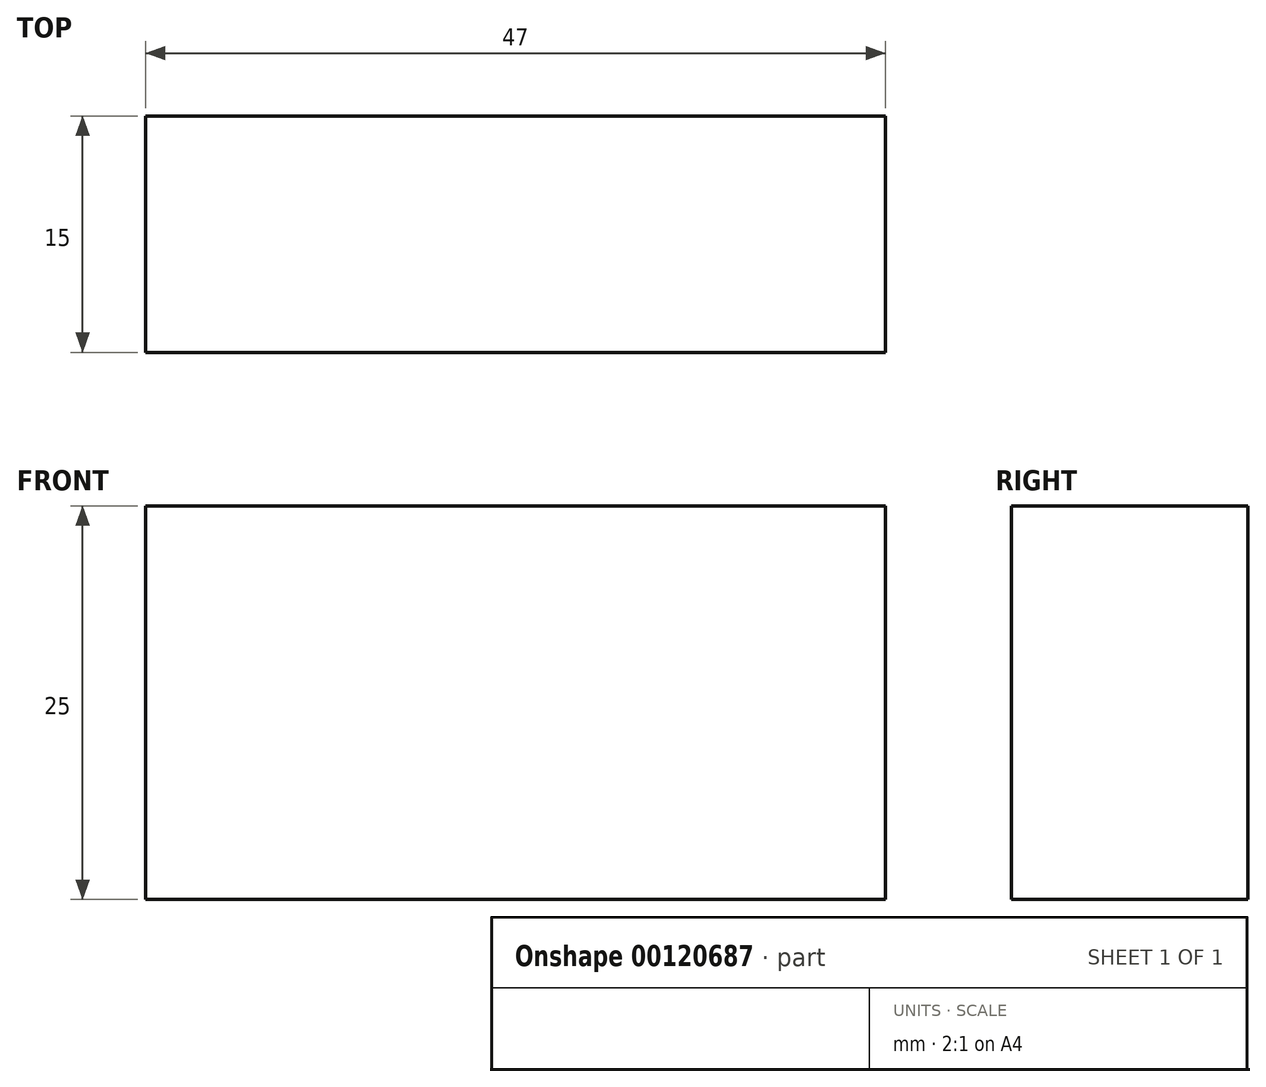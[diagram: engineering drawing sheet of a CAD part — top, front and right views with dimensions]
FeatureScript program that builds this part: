
annotation { "Feature Type Name" : "Feature", "Feature Type Description" : "" }
export const myFeature = defineFeature(function(context is Context, id is Id, definition is map)
    precondition{}
    {
        {
            var Q0;
            Q0=qCreatedBy(makeId("Front.planeOp"),FACE);
            var sketch = newSketch(context, id + "F0", { "sketchPlane" : qUnion([Q0])});
            skLineSegment(sketch, "E0.bottom", {"start": v(-21.17, -4) * mm, "end": v(25.83, -4) * mm});
            skLineSegment(sketch, "E0.top", {"start": v(-21.17, -29) * mm, "end": v(25.83, -29) * mm});
            skLineSegment(sketch, "E0.left", {"start": v(-21.17, -4) * mm, "end": v(-21.17, -29) * mm});
            skLineSegment(sketch, "E0.right", {"start": v(25.83, -4) * mm, "end": v(25.83, -29) * mm});
            skSolve(sketch);
        }
        {
            var Q0;
            Q0 = qSketchRegion(id + "F0", true);
            extrude(context, id + "F1", {"entities" : qUnion([Q0]), "depth" : 15 * mm});
        }
    });
